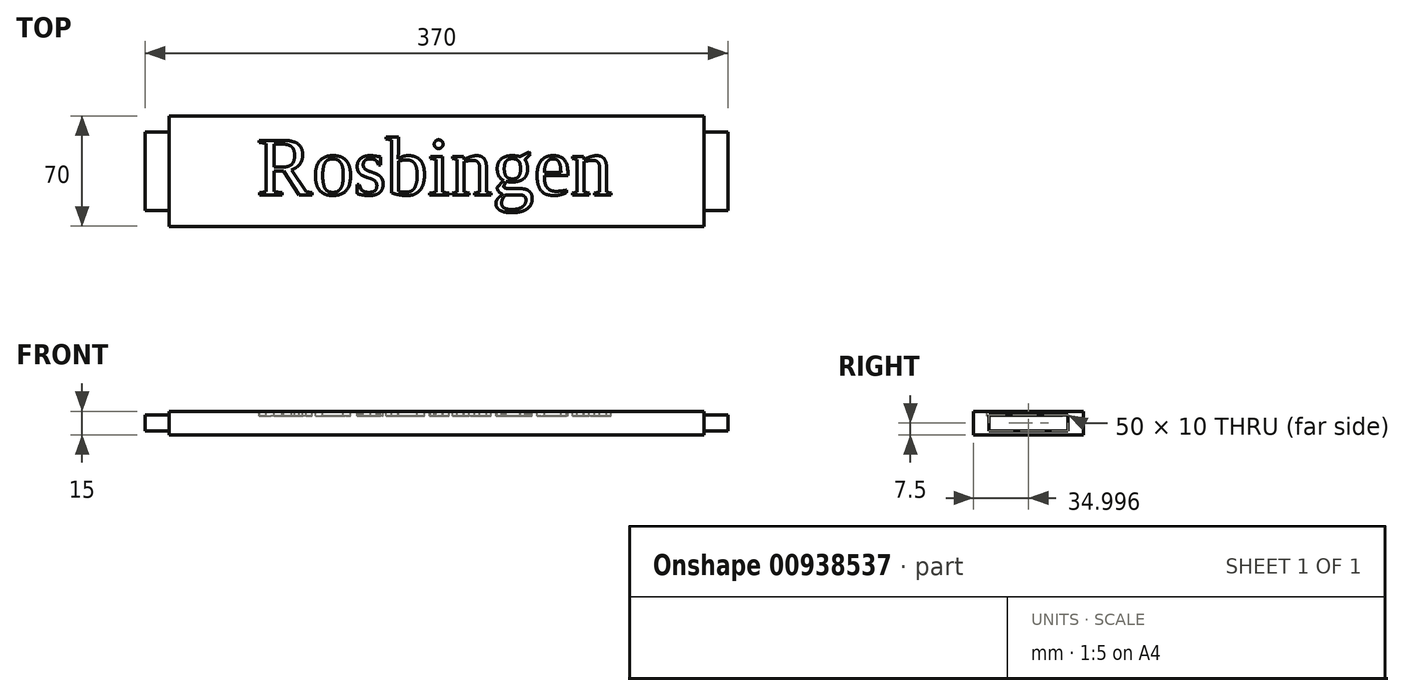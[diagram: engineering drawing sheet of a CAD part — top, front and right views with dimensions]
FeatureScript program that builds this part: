
annotation { "Feature Type Name" : "Feature", "Feature Type Description" : "" }
export const myFeature = defineFeature(function(context is Context, id is Id, definition is map)
    precondition{}
    {
        {
            var Q0;
            Q0=qCreatedBy(makeId("Top.planeOp"),FACE);
            var sketch = newSketch(context, id + "F0", { "sketchPlane" : qUnion([Q0])});
            skLineSegment(sketch, "E0.bottom", {"start": v(-168.85, 80.75) * mm, "end": v(171.15, 80.75) * mm});
            skLineSegment(sketch, "E0.top", {"start": v(-168.85, 10.75) * mm, "end": v(171.15, 10.75) * mm});
            skLineSegment(sketch, "E0.left", {"start": v(-168.85, 80.75) * mm, "end": v(-168.85, 10.75) * mm});
            skLineSegment(sketch, "E0.right", {"start": v(171.15, 80.75) * mm, "end": v(171.15, 10.75) * mm});
            skLineSegment(sketch, "E1", {"start": v(1.15, 10.75) * mm, "end": v(1.15, 80.75) * mm, "construction": true});
            skSolve(sketch);
        }
        {
            var Q0;
            Q0 = qSketchRegion(id + "F0", true);
            extrude(context, id + "F1", {"entities" : qUnion([Q0]), "depth" : 15 * mm, "offsetDistance" : 25 * mm});
        }
        {
            var Q0;
            Q0=makeQuery(id+"F1.opExtrude","SWEPT_FACE",FACE,{"disambiguationData":[OSD([sQuery(id+"F0.wireOp",EDGE,"E0.right")])]});
            var sketch = newSketch(context, id + "F2", { "sketchPlane" : qUnion([Q0])});
            skLineSegment(sketch, "E2.bottom", {"start": v(20.75, 12.5) * mm, "end": v(70.75, 12.5) * mm});
            skLineSegment(sketch, "E2.top", {"start": v(20.75, 2.5) * mm, "end": v(70.75, 2.5) * mm});
            skLineSegment(sketch, "E2.left", {"start": v(20.75, 12.5) * mm, "end": v(20.75, 2.5) * mm});
            skLineSegment(sketch, "E2.right", {"start": v(70.75, 12.5) * mm, "end": v(70.75, 2.5) * mm});
            skSolve(sketch);
        }
        {
            var Q0;
            Q0 = qSketchRegion(id + "F2", true);
            extrude(context, id + "F3", {"entities" : qUnion([Q0]), "operationType" : NewBodyOperationType.ADD, "depth" : 15 * mm, "offsetDistance" : 25 * mm});
        }
        {
            var Q0;
            Q0=makeQuery(id+"F1.opExtrude","SWEPT_FACE",FACE,{"disambiguationData":[OSD([sQuery(id+"F0.wireOp",EDGE,"E0.left")])]});
            var sketch = newSketch(context, id + "F4", { "sketchPlane" : qUnion([Q0])});
            skLineSegment(sketch, "E3.bottom", {"start": v(-70.75, 12.5) * mm, "end": v(-20.75, 12.5) * mm});
            skLineSegment(sketch, "E3.top", {"start": v(-70.75, 2.5) * mm, "end": v(-20.75, 2.5) * mm});
            skLineSegment(sketch, "E3.left", {"start": v(-70.75, 12.5) * mm, "end": v(-70.75, 2.5) * mm});
            skLineSegment(sketch, "E3.right", {"start": v(-20.75, 12.5) * mm, "end": v(-20.75, 2.5) * mm});
            skSolve(sketch);
        }
        {
            var Q0;
            Q0 = qSketchRegion(id + "F4", true);
            extrude(context, id + "F5", {"entities" : qUnion([Q0]), "operationType" : NewBodyOperationType.ADD, "depth" : 15 * mm, "offsetDistance" : 25 * mm});
        }
        {
            var Q0;
            Q0=makeQuery(id+"F1.opExtrude","CAP_FACE",FACE,{"disambiguationData":[OSD([sQuery(id+"F0.wireOp",EDGE,"E0.bottom"),sQuery(id+"F0.wireOp",EDGE,"E0.top"),sQuery(id+"F0.wireOp",EDGE,"E0.left"),sQuery(id+"F0.wireOp",EDGE,"E0.right")])],"isStart":false});
            var sketch = newSketch(context, id + "F6", { "sketchPlane" : qUnion([Q0])});
            skText(sketch, "E4", { "text": "Rosbingen", "fontName": "Tinos-Regular.ttf"});
            skLineSegment(sketch, "E5", {"start": v(1.15, 80.75) * mm, "end": v(1.15, 10.75) * mm, "construction": true});
            const initialGuessF6  = {"E4": [-0.113, 0.03075, 1, 0, 0.038]};
            skSetInitialGuess(sketch, initialGuessF6);
            skSolve(sketch);
        }
        {
            var Q0;
            Q0 = qSketchRegion(id + "F6", true);
            extrude(context, id + "F7", {"entities" : qUnion([Q0]), "operationType" : NewBodyOperationType.REMOVE, "oppositeDirection" : true, "depth" : 3 * mm, "offsetDistance" : 25 * mm});
        }
    });
